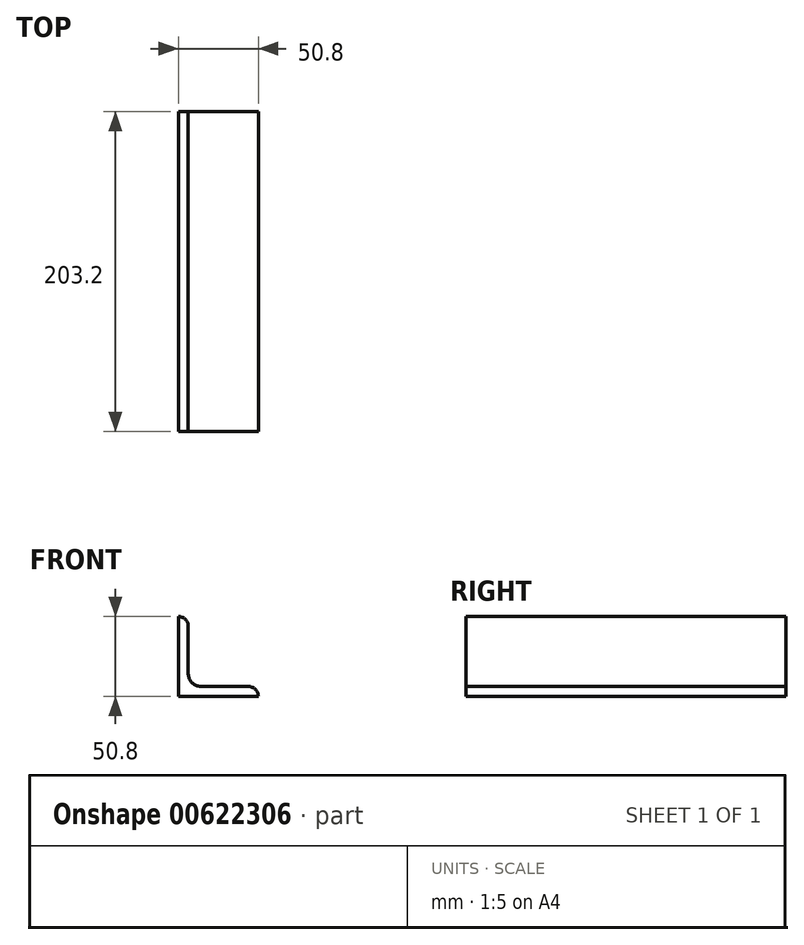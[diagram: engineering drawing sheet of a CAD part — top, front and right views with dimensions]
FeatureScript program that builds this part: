
annotation { "Feature Type Name" : "Feature", "Feature Type Description" : "" }
export const myFeature = defineFeature(function(context is Context, id is Id, definition is map)
    precondition{}
    {
        {
            var Q0;
            Q0=qCreatedBy(makeId("Front.planeOp"),FACE);
            var sketch = newSketch(context, id + "F0", { "sketchPlane" : qUnion([Q0])});
            skLineSegment(sketch, "E0", {"start": v(0, 0) * mm, "end": v(0, 50.8) * mm});
            skLineSegment(sketch, "E1", {"start": v(0, 50.8) * mm, "end": v(0, 50.8) * mm});
            skLineSegment(sketch, "E2", {"start": v(6.35, 44.45) * mm, "end": v(6.35, 14.29) * mm});
            skLineSegment(sketch, "E3", {"start": v(14.29, 6.35) * mm, "end": v(44.45, 6.35) * mm});
            skLineSegment(sketch, "E4", {"start": v(50.8, 0) * mm, "end": v(50.8, 0) * mm});
            skLineSegment(sketch, "E5", {"start": v(50.8, 0) * mm, "end": v(0, 0) * mm});
            skPoint(sketch, "E6.visualSharp", {"position": v(6.35, 50.8) * mm});
            skArc(sketch, "E6.filletArc", {"start": v(6.35, 44.45) * mm, "mid": v(4.5, 48.94) * mm, "end": v(0, 50.8) * mm});
            skPoint(sketch, "E7.visualSharp", {"position": v(50.8, 6.35) * mm});
            skArc(sketch, "E7.filletArc", {"start": v(50.8, 0) * mm, "mid": v(48.94, 4.5) * mm, "end": v(44.45, 6.35) * mm});
            skPoint(sketch, "E8.visualSharp", {"position": v(6.35, 6.35) * mm});
            skArc(sketch, "E8.filletArc", {"start": v(6.35, 14.29) * mm, "mid": v(8.67, 8.67) * mm, "end": v(14.29, 6.35) * mm});
            skSolve(sketch);
        }
        {
            var Q0;
            Q0=makeQuery(id+"F0.imprint","IMPRINT",FACE,{"disambiguationData":[TD([[makeQuery(id+"F0.imprint","IMPRINT",EDGE,{"derivedFrom":sQuery(id+"F0.wireOp",EDGE,"E0")}),-1.0]])]});
            extrude(context, id + "F1", {"entities" : qUnion([Q0]), "depth" : 203.2 * mm, "offsetDistance" : 25.4 * mm});
        }
    });
